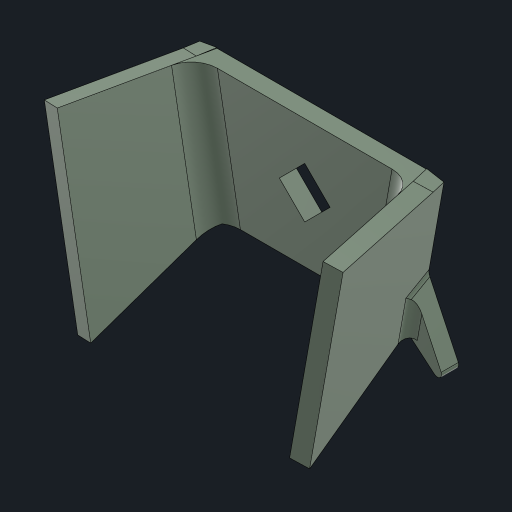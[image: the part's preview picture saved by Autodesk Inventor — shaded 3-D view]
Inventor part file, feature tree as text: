
AUTODESK INVENTOR PART (.ipt)
format: ipt  version: 2023 (Build 270158000, 158)  size: 424,448 bytes
history: native  units: mm
features: extrude x23, sketch x17, other x13, projected_geometry x3, fillet x2, mirror x1
ambient origin geometry x8: Origin, YZ Plane, XZ Plane, XY Plane, X Axis, Y Axis, Z Axis, Center Point
bodies: Body1 (feature_tree)
feature tree (59):
  other  "ソリッド1"
  extrude  "押し出し1"  Depth=0.261799mm
  other  "作業平面1"
  other  "作業平面3"
  extrude  "押し出し5"  Depth=37.0mm
  extrude  "押し出し6"  Depth=25.0mm
  other  "おでこ"
  other  "作業平面4"
  extrude  "押し出し7"  Depth=22.68928mm
  other  "作業平面5"
  extrude  "押し出し8"  Depth=1.658063mm
  extrude  "押し出し9"  Depth=60.0mm
  other  "作業平面9"
  extrude  "押し出し16"  Depth=3.0mm
  other  "作業平面11"
  extrude  "押し出し11"  Depth=80.0mm
  extrude  "押し出し12"  Depth=180.0mm
  extrude  "押し出し13"  Depth=25.0mm
  extrude  "押し出し15"  Depth=5.0mm
  extrude  "右半分"  Depth=180.0mm
  other  "作業平面12"
  extrude  "押し出し17"  Depth=15.0mm
  other  "作業平面13"
  other  "作業平面14"
  other  "作業平面15"
  other  "作業平面16"
  sketch  "スケッチ18"
  extrude  "押し出し18"  Depth=50.0mm TaperAngle=0.0deg
  sketch  "スケッチ19"
  extrude  "押し出し19"  Depth=50.0mm
  sketch  "スケッチ20"
  extrude  "押し出し20"  Depth=25.0mm TaperAngle=90.0deg
  extrude  "押し出し21"  Depth=13.962634mm
  extrude  "押し出し22"  Depth=11.34464mm
  extrude  "押し出し23"  Depth=10.0mm TaperAngle=0.0deg
  extrude  "押し出し24"  Depth=10.0mm TaperAngle=0.0deg
  extrude  "押し出し25"  Depth=8.0mm
  extrude  "押し出し26"  Depth=15.0mm TaperAngle=0.0deg
  fillet  "フィレット1"  Radius=15.0mm
  extrude  "爪"  TaperAngle=0.0deg  [1 undecoded]
  mirror  "ミラー1"
  fillet  "フィレット3"  Radius=4.0mm
  sketch  "スケッチ1"
  sketch  "スケッチ5"
  sketch  "スケッチ6"
  sketch  "スケッチ8"
  sketch  "スケッチ9"
  sketch  "スケッチ10"
  projected_geometry  "投影ループ1"
  projected_geometry  "投影ループ2"
  sketch  "スケッチ12"
  sketch  "スケッチ14"
  sketch  "スケッチ16"
  projected_geometry  "投影ループ3"
  sketch  "スケッチ17"
  sketch  "スケッチ21"
  sketch  "スケッチ22"
  sketch  "スケッチ23"
  sketch  "スケッチ24"
note: 1 required parameter value undecoded (feature->parameter linkage not recoverable at this tier; creation-order binding heuristic only, values carry confidence <= 0.55)
